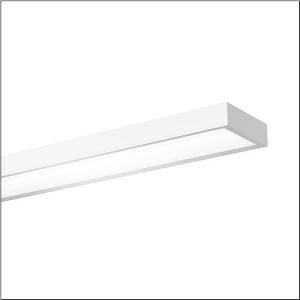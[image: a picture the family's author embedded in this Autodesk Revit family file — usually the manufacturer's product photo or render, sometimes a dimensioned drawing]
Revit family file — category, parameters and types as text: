
# Revit family: sport_31_51hs12dc4eca
name_source: partatom
category: Lighting Fixtures
units: mm (PartAtom-declared; Revit-internal decimal feet)

## family parameters
Cut with Voids When Loaded = No
Host = Face
Light Source = No
Part Type = Normal
Room Calculation Point = No
Round Connector Dimension = Use Diameter
Shared = No

## types (1)
- --- (1 x LED, 11990 lm, 89.4 W, 4000K)
    Apparent Load = 89 VA
    CIE Flux Codes = 65 89 97 100 100
    Color Rendering = 80
    Color Temperature = 4000K
    Default Elevation = 1800 mm
    Description = Sport 31, LED high bay luminaire, primary light control with reflector, of sheet steel, primary anti-glare with prismatic structure, of PC, primary optical cover: cover panel, of PC, light emission: direct distribution, primary light characteristic: symmetric, installation type: suspended mounting, recessed, surface-mounted, LED, rated luminous flux: 12.000lm, luminous efficacy: 137lm/W, light colour: 840, colour temperature: 4000K, control gear: ECG DALI, with terminal, 5-pole, max. 2.5mm², mains connection: 220..240V, AC/DC, 50/60Hz, rated input power: 88W, housing, of sheet steel, traffic white (RAL 9016), length: 1.540mm, width: 315mm, height: 95mm, protection rating (complete): IP20, protection rating (lamp compartment, on room side): IP50, insulation class (complete): insulation class I (protective earthing), certification: CE, ENEC, UKCA, ball protection: ball impact resistant with ceiling mounting or chain suspension, impact resistance: IK08, permissible operating ambient temperature: -20..+35°C, standard: DIN 18032-3, EN 60598-2-22, packaging unit: 1 piece
    Height = 100 mm  [stored 0.328084 ft]
    Lamp = 1 x LED
    Lamp Light Flux = 11990 lm
    Lamp Power = 89.4 W
    Lamp count = 1
    Length = 1500 mm
    Luminous efficacy = 134 lm/W
    Manufacturer = Siteco
    ModVariant = No
    Model = 51HS12DC4ECA
    Mounting Place = Ceiling
    Mounting Type = Pendant
    Number of Poles = 1
    OnlyDefault = Yes
    Power Factor = 1
    Product Name = Sport 31
    Product group = LED high bay luminaire
    ProductGroupID = 903
    Protection Class = Protection class I
    Protection Degree = IP 20
    RLX_Detail_Level = 1
    RLX_Emergency_Light_Flux = 0 lm
    RLX_Emergency_Type = 0
    RLX_Emergency_Type_DB = No
    RlxData = <blob elided: 22857 chars, md5=e0f85f62>
    Socket = socket
    Standby Power = 0 W
    System Light Flux = 11990 lm
    System Power = 89 W
    Type Comments = factory setting: luminous flux: 100 % | dim-lin: 254 | 380 mA
    Type Image = l_1006823.jpg
    URL = http://relux.com
    VarID = @adj_133049
    Voltage = 0 V
    Weight = 0.00 kg
    Width = 315 mm

note: [stored X ft] marks values corroborated as IEEE doubles in the binary element streams (Revit-internal decimal feet)

## geometry (parser evidence)
native form markers: Blend x4, Sweep x10
no freeform markers — native parametric forms only
